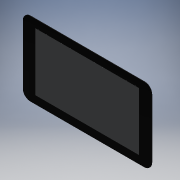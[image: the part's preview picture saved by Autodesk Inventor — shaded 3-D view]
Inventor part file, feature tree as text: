
AUTODESK INVENTOR PART (.ipt)
format: ipt  version: 2018 (Build 220112000, 112)  size: 220,672 bytes
history: native  units: in
note: dims shown in document units (in); Inventor stores cm internally (conversion verified against a paired STEP export)
features: extrude x4, sketch x4, chamfer x1
ambient origin geometry x8: Origin, YZ Plane, XZ Plane, XY Plane, X Axis, Y Axis, Z Axis, Center Point
bodies: Body1 (feature_tree)
feature tree (9):
  extrude  "Extrusion2"  Depth=4.3606in
  extrude  "Extrusion3"  Depth=2.1803in
  extrude  "Extrusion4"  Depth=0.0394in TaperAngle=0.0deg
  chamfer  "Chamfer1"  Distance=3.9606in
  extrude  "Extrusion5"  Depth=0.0004in
  sketch  "Sketch1"  dims[d0=7.5969in d1=4.3606in]
  sketch  "Sketch3"  dims[d2=3.7984in d3=2.1803in]
  sketch  "Sketch4"  dims[d6=0.4331in d7=0.0394in d8=0.0in]
  sketch  "Sketch5"  dims[d9=6.5433in d10=3.9606in d12=3.2717in d13=0.261in d14=0.1953in d15=0.0in d16=0.5906in d17=0.315in d18=0.1181in d19=0.7874in d20=0.7874in d22=4.9685in d23=0.7874in d25=2.5846in d29=0.0984in d30=0.8189in d32=1.9075in d33=0.8496in d42=0.7874in d44=2.2835in d45=0.7874in d47=1.9291in d50=0.0984in d51=0.0in d52=0.0984in d53=0.125in d54=45.0deg d55=6.1024in d56=3.4252in d57=1.7126in d58=3.0512in d59=0.0004in d60=0.0in]
